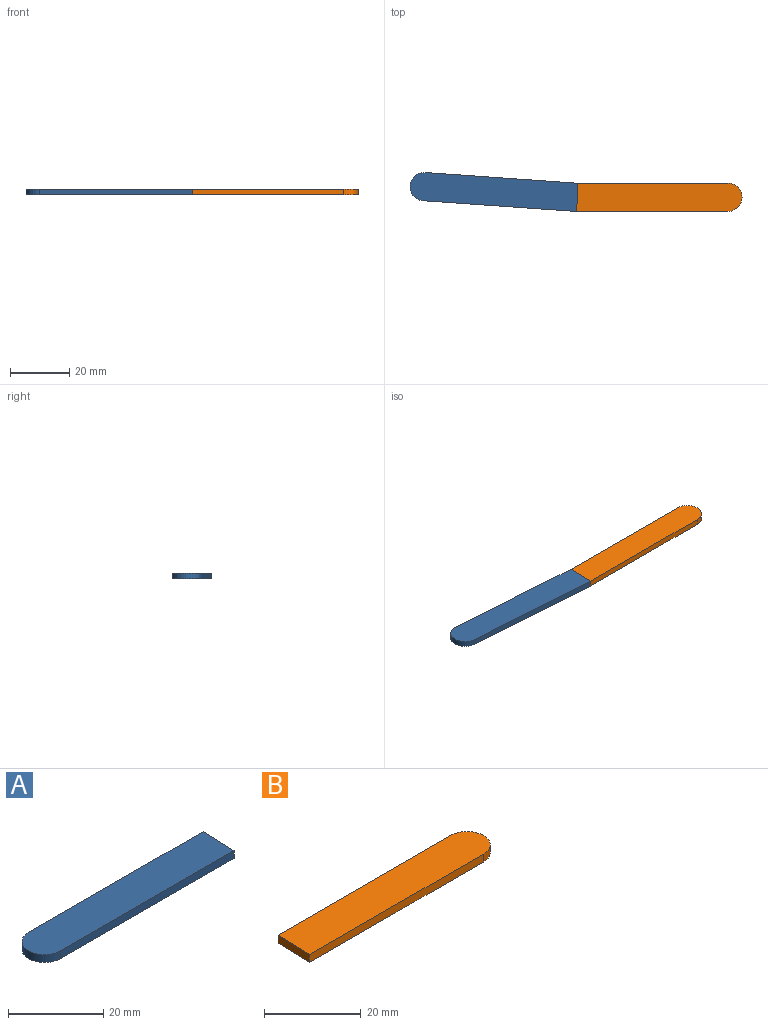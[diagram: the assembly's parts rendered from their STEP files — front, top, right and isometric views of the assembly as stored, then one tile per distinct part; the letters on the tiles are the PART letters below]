
ASSEMBLY  parts=2 mates=1
PART A: 6 faces, bbox 56.7x9.5x2 mm
  f0: cylinder r=4.76mm len=9.53mm, axis (0,0,-1), area 29.9mm2, adj f1,f3,f4,f5
  f1: plane 51.59x2mm, normal (0,-1,0), area 103.2mm2, adj f0,f2,f4,f5
  f2: plane 9.53x2mm, normal (1,-0.03,0), area 19.1mm2, adj f1,f3,f4,f5
  f3: plane 51.93x2mm, normal (0,1,0), area 103.9mm2, adj f0,f2,f4,f5
  f4: plane 56.69x9.53mm, normal (0,0,1), area 528.6mm2, adj f0,f1,f2,f3
  f5: plane 56.69x9.53mm, normal (0,0,-1), area 528.6mm2, adj f0,f1,f2,f3
PART B: 6 faces, bbox 55.7x9.5x2 mm
  f0: plane 9.53x2mm, normal (-1,0.03,0), area 19.1mm2, adj f1,f3,f4,f5
  f1: plane 50.96x2mm, normal (0,-1,0), area 101.9mm2, adj f0,f2,f4,f5
  f2: cylinder r=4.76mm len=9.53mm, axis (0,0,-1), area 29.9mm2, adj f1,f3,f4,f5
  f3: plane 50.63x2mm, normal (0,1,0), area 101.3mm2, adj f0,f2,f4,f5
  f4: plane 55.72x9.53mm, normal (0,0,1), area 519.4mm2, adj f0,f1,f2,f3
  f5: plane 55.72x9.53mm, normal (0,0,-1), area 519.4mm2, adj f0,f1,f2,f3
PLACE A rot(axis=(-1,0.03,0),180deg) t=(4.97,-662.73,-6.6)mm
PLACE B t=(27.84,10.34,-8.6)mm fixed
MATE fastened B.f0 <-> A.f2  axis (-1,0.03,0) through (-370.52,-312.67,-7.6)mm
